# Revit family: cLighting - Luminii - Stenos - Suspended Track Master Assembly
name_source: partatom
category: Lighting Fixtures
units: mm (PartAtom-declared; Revit-internal decimal feet)

## family parameters
Cut with Voids When Loaded = No
Host = Face
Light Source = No
OmniClass Number = 23.80.70.11.14.21
OmniClass Title = Spots and Tracklight Specialties
Part Type = Normal
Room Calculation Point = No
Round Connector Dimension = Use Diameter
Shared = Yes

## types (3) — shared parameters
Apparent Load = 4 VA
Assembly Code = D5020230
C Hanging Wire Side Offset = 1.13 "
Depth = 1 "
Description = Suspended Trim Track System
Environment = Indoor
Finish = Metal - Luminii - Silver Anodized Aluminum
Frequency = 60 Hz
Keynote = 26 50 00
Load Classification = Lighting
Manufacturer = Luminii
Model = STH
Number of Poles = 1
Phase = 1
Power Factor = 1
Power Source Type = Driver
Product Page URL = https://www.luminii.com
URL = https://www.luminii.com
Version = 2020 - v1.0a
Voltage = 120 V
Voltage Comments = 120-277VAC
Warranty URL = https://www.luminii.com
Wattage Comments = 96W max on track
Width = 0.95 "
zero-valued in all types: Default Elevation

## per-type parameters (varying)
| type | Constraints | Current Amps | Length |
| Stenos Suspended - 4' | 1 | 4 A | 48 " |
| Stenos Suspended - 8' | 2 | 50 A | 96 " |
| Stenos Suspended - 12' | 3 | 50 A | 144 " |

## geometry (parser evidence)
native form markers: Sweep x9
no freeform markers — native parametric forms only
